# Revit family: Tank_Rheem_HotWaterStorage
name_source: partatom
category: Mechanical Equipment
revit_build: Autodesk Revit 2014 (Build: 20140709_2115(x64)
units: mm (PartAtom-declared; Revit-internal decimal feet)

## types (1)
- This Family Using Type Catalogue
    1 = 1535 mm
    ApparentPower = 0 kW
    AvailableHeatingUnitRating = 0 kW
    D = 510 mm  [stored 1.67323 ft]
    Dis = 400 mm  [stored 1.31234 ft]
    DrainDiameter = 50 mm  [stored 0.164042 ft]
    DrainInstalled = Yes
    DrainRadius = 25 mm  [stored 0.082021 ft]
    DryWeight_ANZRS = 115.00 kg
    E = 1435 mm  [stored 4.70801 ft]
    ExpectedServiceLifeYears = 0
    F = 417 mm  [stored 1.36811 ft]
    FlangeDistance = 360 mm
    FluidDensity = 0.0000 kg/m³
    FluidTemperatureMax = 0 °C
    FluidTemperatureMin = 0 °C
    FluidType = Water
    FullLoadAmps = 0 A
    G = 879 mm  [stored 2.88386 ft]
    H = 1341 mm  [stored 4.39961 ft]
    InOutDistance = 360 mm
    InletOutletDiameter = 50 mm  [stored 0.164042 ft]
    InletOutletFlowRate_ANZRS = 0.0 L/s
    InletOutletRadius = 25 mm  [stored 0.082021 ft]
    J = 1803 mm  [stored 5.91535 ft]
    LegDistance = 160 mm  [stored 0.524934 ft]
    Length = 350 mm  [stored 1.14829 ft]
    Manufacturer = Rheem Solahart
    Max_SupplyPressure_ANZRS = 680.0 Pa
    Model = 1000
    MotorPoles = 0
    MotorSize = 0 kW
    NCC_SEC_J_Compliance = Yes
    OperatingMass = 0.00 kg
    OperatingPressure_ANZRS = 850.0 Pa
    OperatingTempMax = 90 °C
    OperatingTempMin = 0 °C
    Potable = Yes
    PowerFactor = 1
    PowerSource = AC
    PressureReleaseValveInstalled = Yes
    R1 = 645 mm  [stored 2.11614 ft]
    RunLoadAmps = 0 A
    ShippingMass = 0.00 kg
    StorageVolume_ANZRS = 920.0 L
    SupplyFrequency = 50/60 Hz
    SupplyPhase = 1
    SupplyVoltage = 415 V
    TankDiaWithInsulation = 1000 mm  [stored 3.28084 ft]
    TankDiameter = 800 mm  [stored 2.62467 ft]
    TankHeight = 2220 mm  [stored 7.28346 ft]
    TankMaterial = <By Category>
    TankRadius = 400 mm  [stored 1.31234 ft]
    VentInstalled = No
    WarrantyDurationMonths = 0
    WetWeight_ANZRS = 1035.00 kg
    Width = 350 mm  [stored 1.14829 ft]

note: [stored X ft] marks values corroborated as IEEE doubles in the binary element streams (Revit-internal decimal feet)

## geometry (parser evidence)
native form markers: Sweep x7
no freeform markers — native parametric forms only
